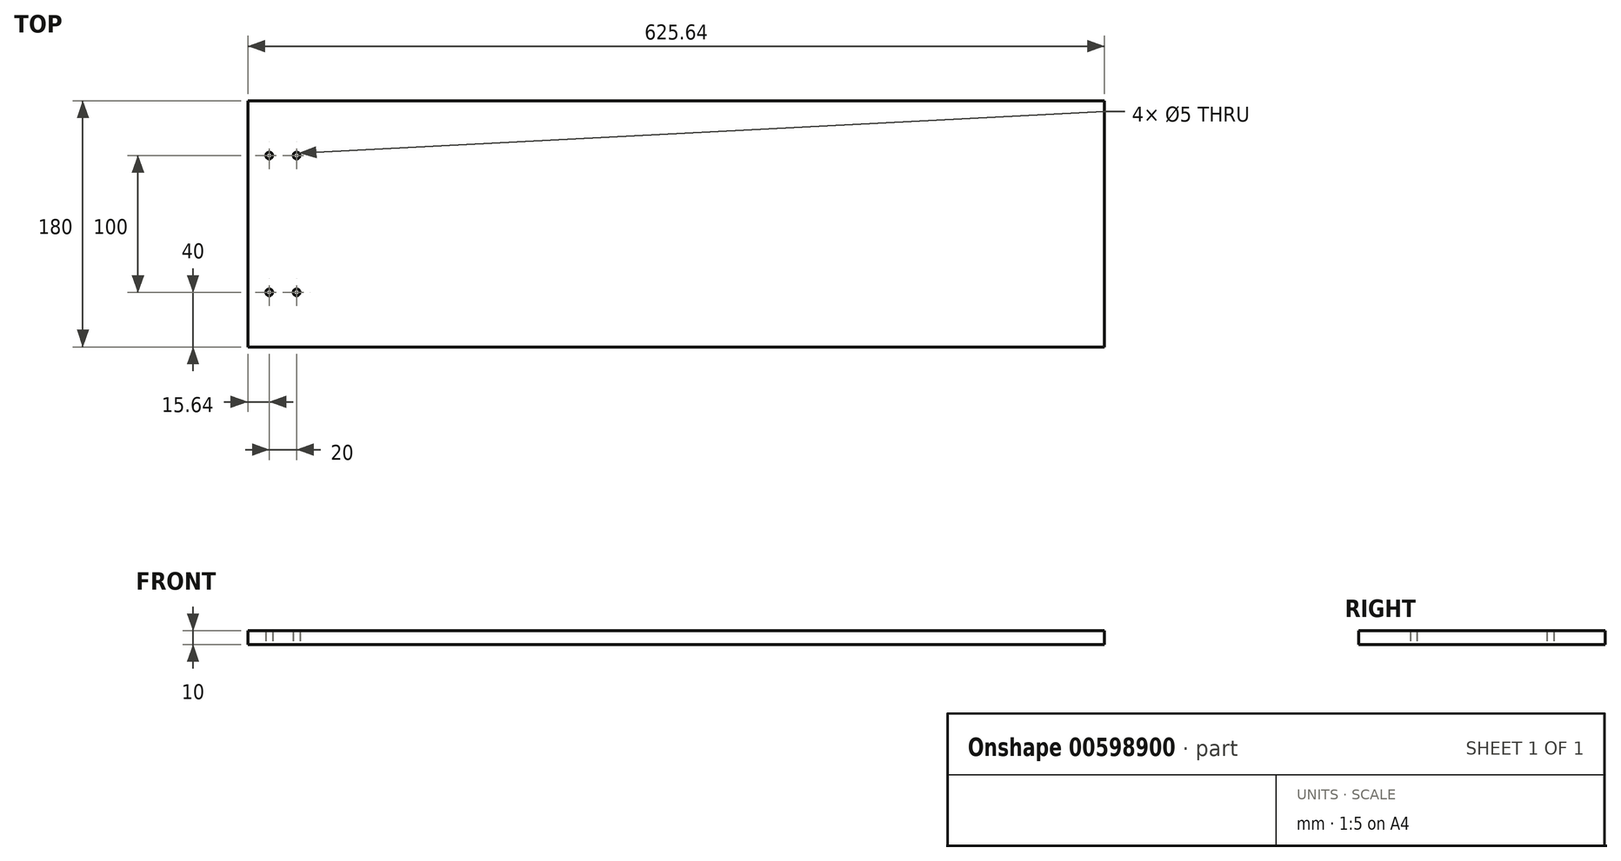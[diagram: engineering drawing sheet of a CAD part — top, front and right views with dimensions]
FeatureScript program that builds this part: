
annotation { "Feature Type Name" : "Feature", "Feature Type Description" : "" }
export const myFeature = defineFeature(function(context is Context, id is Id, definition is map)
    precondition{}
    {
        {
            var Q0;
            Q0=qCreatedBy(makeId("Top.planeOp"),FACE);
            var sketch = newSketch(context, id + "F0", { "sketchPlane" : qUnion([Q0])});
            skLineSegment(sketch, "E0.bottom", {"start": v(0, 0) * mm, "end": v(620, 0) * mm});
            skLineSegment(sketch, "E0.top", {"start": v(0, -180) * mm, "end": v(620, -180) * mm});
            skLineSegment(sketch, "E0.left", {"start": v(0, 0) * mm, "end": v(0, -180) * mm});
            skLineSegment(sketch, "E0.right", {"start": v(620, 0) * mm, "end": v(620, -180) * mm});
            skSolve(sketch);
        }
        {
            var Q0;
            Q0 = qSketchRegion(id + "F0", true);
            extrude(context, id + "F1", {"entities" : qUnion([Q0]), "depth" : 10 * mm, "offsetDistance" : 25 * mm});
        }
        {
            var Q0;
            Q0=makeQuery(id+"F1.opExtrude","CAP_FACE",FACE,{"disambiguationData":[OSD([sQuery(id+"F0.wireOp",EDGE,"E0.bottom"),sQuery(id+"F0.wireOp",EDGE,"E0.top"),sQuery(id+"F0.wireOp",EDGE,"E0.left"),sQuery(id+"F0.wireOp",EDGE,"E0.right")])],"isStart":false});
            var sketch = newSketch(context, id + "F2", { "sketchPlane" : qUnion([Q0])});
            skLineSegment(sketch, "E1", {"start": v(0, -40) * mm, "end": v(30, -40) * mm, "construction": true});
            skLineSegment(sketch, "E2", {"start": v(0, -140) * mm, "end": v(30, -140) * mm, "construction": true});
            skPoint(sketch, "E3", {"position": v(10, -40) * mm});
            skPoint(sketch, "E4", {"position": v(10, -140) * mm});
            skSolve(sketch);
        }
        {
            var Q0;
            Q0=sQuery(id+"F2.wireOp",VERTEX,"E3");
            var Q1;
            Q1=sQuery(id+"F2.wireOp",VERTEX,"E1.end");
            var Q2;
            Q2=sQuery(id+"F2.wireOp",VERTEX,"E4");
            var Q3;
            Q3=sQuery(id+"F2.wireOp",VERTEX,"E2.end");
            var Q4;
            Q4=makeQuery(id+"F1.opExtrude","SWEPT_BODY",BODY,{"disambiguationData":[OSD([sQuery(id+"F0.wireOp",EDGE,"E0.bottom"),sQuery(id+"F0.wireOp",EDGE,"E0.top"),sQuery(id+"F0.wireOp",EDGE,"E0.left"),sQuery(id+"F0.wireOp",EDGE,"E0.right")])]});
            hole(context, id + "F3", {"style" : HoleStyle.SIMPLE, "endStyle" : HoleEndStyle.BLIND, "holeDiameter" : 5 * mm, "majorDiameter" : 5 * mm, "holeDepth" : 11 * mm, "isTappedThrough" : true, "tappedDepth" : 12 * mm, "tapClearance" : 3, "startFromSketch" : true, "locations" : qUnion([Q0, Q1, Q2, Q3]), "scope" : qUnion([Q4])});
        }
        {
            var Q0;
            Q0=makeQuery(id+"F1.opExtrude","SWEPT_FACE",FACE,{"disambiguationData":[OSD([sQuery(id+"F0.wireOp",EDGE,"E0.left")])]});
            extrude(context, id + "F4", {"entities" : qUnion([Q0]), "operationType" : NewBodyOperationType.ADD, "depth" : 5.64 * mm, "offsetDistance" : 25 * mm});
        }
    });
